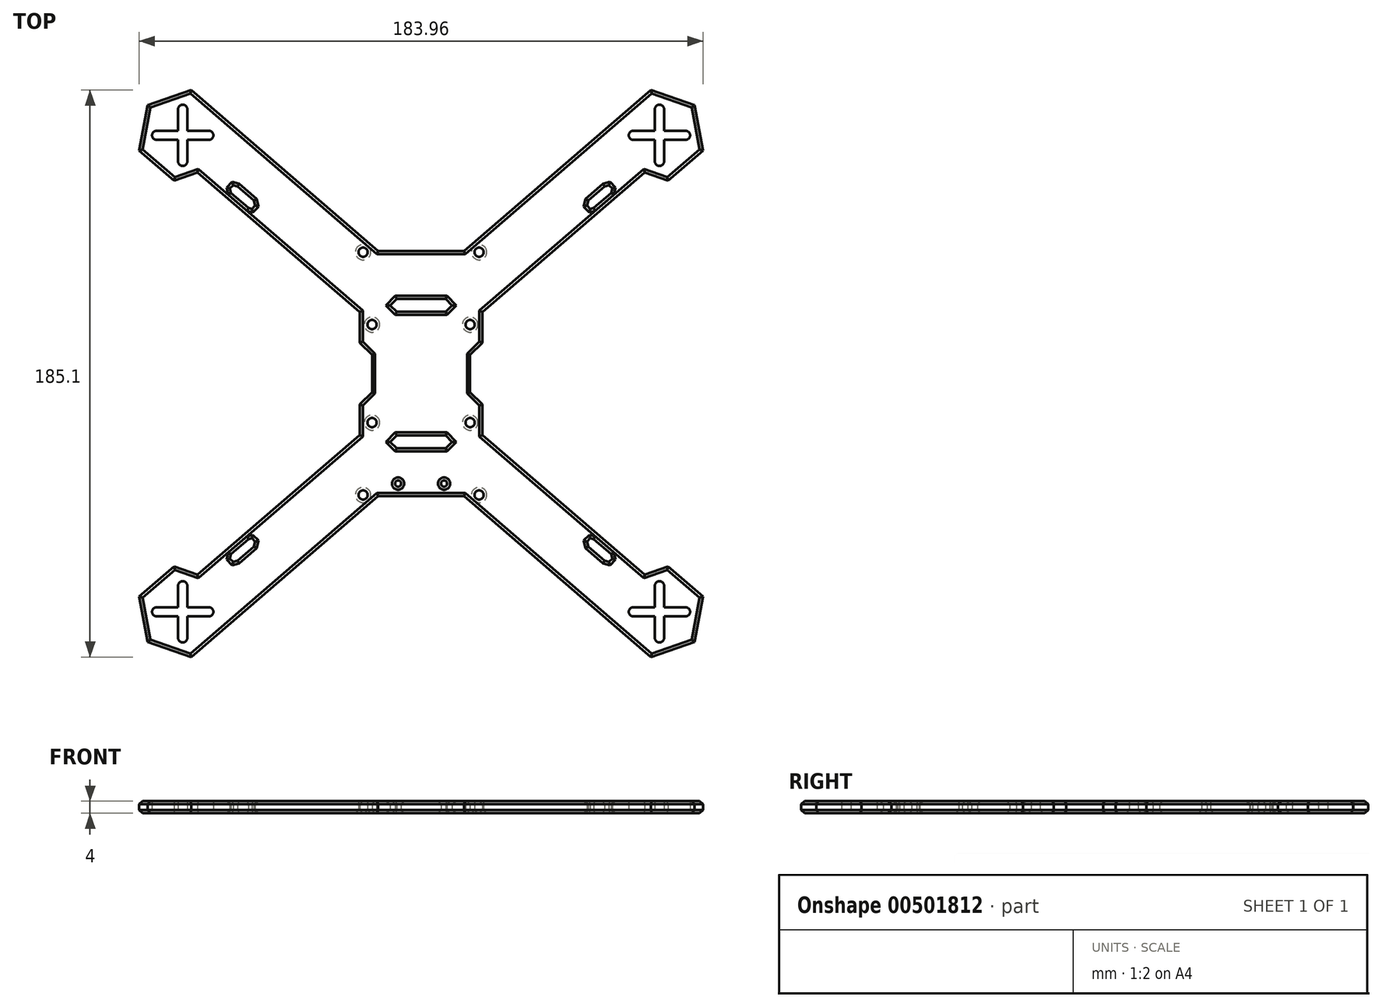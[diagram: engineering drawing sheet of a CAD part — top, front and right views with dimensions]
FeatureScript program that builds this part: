
annotation { "Feature Type Name" : "Feature", "Feature Type Description" : "" }
export const myFeature = defineFeature(function(context is Context, id is Id, definition is map)
    precondition{}
    {
        {
            var Q0;
            Q0=qCreatedBy(makeId("Top.planeOp"),FACE);
            var sketch = newSketch(context, id + "F0", { "sketchPlane" : qUnion([Q0])});
            skCircle(sketch, "E0", {"center": v(16, 16) * mm, "radius": 1.5 * mm});
            skPoint(sketch, "E1.middle", {"position": v(77.78, 77.78) * mm});
            skLineSegment(sketch, "E2.bottom", {"start": v(77.78, 67.78) * mm, "end": v(77.78, 67.78) * mm});
            skLineSegment(sketch, "E2.top", {"start": v(77.78, 87.78) * mm, "end": v(77.78, 87.78) * mm});
            skLineSegment(sketch, "E2.left", {"start": v(76.28, 69.28) * mm, "end": v(76.28, 76.29) * mm});
            skLineSegment(sketch, "E2.right", {"start": v(79.28, 69.28) * mm, "end": v(79.28, 76.28) * mm});
            skLineSegment(sketch, "E3.bottom", {"start": v(86.28, 79.28) * mm, "end": v(79.28, 79.28) * mm});
            skLineSegment(sketch, "E3.top", {"start": v(86.28, 76.28) * mm, "end": v(79.28, 76.28) * mm});
            skLineSegment(sketch, "E3.left", {"start": v(87.78, 77.78) * mm, "end": v(87.78, 77.78) * mm});
            skLineSegment(sketch, "E3.right", {"start": v(67.78, 77.78) * mm, "end": v(67.78, 77.78) * mm});
            skPoint(sketch, "E4.visualSharp", {"position": v(79.28, 87.78) * mm});
            skArc(sketch, "E4.filletArc", {"start": v(79.28, 86.28) * mm, "mid": v(78.84, 87.34) * mm, "end": v(77.78, 87.78) * mm});
            skPoint(sketch, "E5.visualSharp", {"position": v(76.28, 87.78) * mm});
            skArc(sketch, "E5.filletArc", {"start": v(77.78, 87.78) * mm, "mid": v(76.72, 87.34) * mm, "end": v(76.28, 86.28) * mm});
            skPoint(sketch, "E6.visualSharp", {"position": v(79.28, 67.78) * mm});
            skArc(sketch, "E6.filletArc", {"start": v(77.78, 67.78) * mm, "mid": v(78.84, 68.22) * mm, "end": v(79.28, 69.28) * mm});
            skPoint(sketch, "E7.visualSharp", {"position": v(76.28, 67.78) * mm});
            skArc(sketch, "E7.filletArc", {"start": v(76.28, 69.28) * mm, "mid": v(76.72, 68.22) * mm, "end": v(77.78, 67.78) * mm});
            skPoint(sketch, "E8.visualSharp", {"position": v(87.78, 79.28) * mm});
            skArc(sketch, "E8.filletArc", {"start": v(87.78, 77.78) * mm, "mid": v(87.34, 78.84) * mm, "end": v(86.28, 79.28) * mm});
            skPoint(sketch, "E9.visualSharp", {"position": v(87.78, 76.28) * mm});
            skArc(sketch, "E9.filletArc", {"start": v(86.28, 76.28) * mm, "mid": v(87.34, 76.72) * mm, "end": v(87.78, 77.78) * mm});
            skPoint(sketch, "E10.visualSharp", {"position": v(67.78, 79.28) * mm});
            skArc(sketch, "E10.filletArc", {"start": v(69.28, 79.28) * mm, "mid": v(68.22, 78.84) * mm, "end": v(67.78, 77.78) * mm});
            skPoint(sketch, "E11.visualSharp", {"position": v(67.78, 76.28) * mm});
            skArc(sketch, "E11.filletArc", {"start": v(67.78, 77.78) * mm, "mid": v(68.22, 76.72) * mm, "end": v(69.28, 76.28) * mm});
            skLineSegment(sketch, "E12.trimOffspring", {"start": v(76.28, 79.28) * mm, "end": v(76.28, 86.28) * mm});
            skLineSegment(sketch, "E13.trimOffspring", {"start": v(76.28, 76.28) * mm, "end": v(69.28, 76.28) * mm});
            skLineSegment(sketch, "E14.trimOffspring", {"start": v(76.28, 79.28) * mm, "end": v(69.28, 79.28) * mm});
            skLineSegment(sketch, "E15.trimOffspring", {"start": v(79.28, 79.28) * mm, "end": v(79.28, 86.28) * mm});
            skLineSegment(sketch, "E16.cCircle", {"start": v(49.17, 49.17) * mm, "end": v(49.17, 49.17) * mm});
            skLineSegment(sketch, "E17", {"start": v(77.78, 77.78) * mm, "end": v(0, 0) * mm, "construction": true});
            skLineSegment(sketch, "E18", {"start": v(69.28, 87.64) * mm, "end": v(14, 40) * mm});
            skLineSegment(sketch, "E19", {"start": v(20, 20.09) * mm, "end": v(72.91, 65.7) * mm});
            skLineSegment(sketch, "E20", {"start": v(20, 20.09) * mm, "end": v(20, 10.04) * mm});
            skLineSegment(sketch, "E21", {"start": v(14, 40) * mm, "end": v(0, 40) * mm});
            skLineSegment(sketch, "E22", {"start": v(61.99, 58.96) * mm, "end": v(56.29, 54.05) * mm});
            skCircle(sketch, "E23", {"center": v(77.78, 77.78) * mm, "radius": 63.5 * mm, "construction": true});
            skLineSegment(sketch, "E24", {"start": v(8, 20.17) * mm, "end": v(0, 20.17) * mm});
            skLineSegment(sketch, "E25", {"start": v(8, 20.17) * mm, "end": v(10.12, 22.3) * mm});
            skLineSegment(sketch, "E26", {"start": v(10.12, 22.3) * mm, "end": v(8, 24.41) * mm});
            skLineSegment(sketch, "E27", {"start": v(8, 24.41) * mm, "end": v(0, 24.41) * mm});
            skLineSegment(sketch, "E28", {"start": v(14, 40) * mm, "end": v(14, 0) * mm, "construction": true});
            skCircle(sketch, "E29", {"center": v(18.94, 39.63) * mm, "radius": 1.5 * mm});
            skLineSegment(sketch, "E30.3", {"start": v(59.86, 61.08) * mm, "end": v(61.31, 61.47) * mm});
            skLineSegment(sketch, "E30.4", {"start": v(61.31, 61.47) * mm, "end": v(62.37, 60.41) * mm});
            skLineSegment(sketch, "E30.5", {"start": v(62.37, 60.41) * mm, "end": v(61.99, 58.96) * mm});
            skLineSegment(sketch, "E31.0", {"start": v(56.29, 54.05) * mm, "end": v(55.18, 53.75) * mm});
            skLineSegment(sketch, "E31.1", {"start": v(55.18, 53.75) * mm, "end": v(54.12, 54.81) * mm});
            skLineSegment(sketch, "E31.2", {"start": v(54.12, 54.81) * mm, "end": v(54.56, 56.5) * mm});
            skLineSegment(sketch, "E32", {"start": v(14, 40) * mm, "end": v(21.57, 46.53) * mm, "construction": true});
            skLineSegment(sketch, "E33", {"start": v(21.57, 46.53) * mm, "end": v(26.14, 41.23) * mm, "construction": true});
            skLineSegment(sketch, "E34", {"start": v(26.14, 41.23) * mm, "end": v(18.57, 34.7) * mm, "construction": true});
            skLineSegment(sketch, "E35", {"start": v(18.57, 34.7) * mm, "end": v(14, 40) * mm, "construction": true});
            skLineSegment(sketch, "E36", {"start": v(59.86, 61.08) * mm, "end": v(54.56, 56.5) * mm});
            skPoint(sketch, "E37.0.midPoint", {"position": v(69.28, 87.64) * mm});
            skCircle(sketch, "E38.cCircle", {"center": v(77.78, 77.78) * mm, "radius": 13.02 * mm, "construction": true});
            skLineSegment(sketch, "E38.0", {"start": v(63.59, 82.74) * mm, "end": v(74.98, 92.55) * mm});
            skLineSegment(sketch, "E38.1", {"start": v(74.98, 92.55) * mm, "end": v(89.17, 87.6) * mm});
            skLineSegment(sketch, "E38.2", {"start": v(89.17, 87.6) * mm, "end": v(91.98, 72.83) * mm});
            skLineSegment(sketch, "E38.3", {"start": v(91.98, 72.83) * mm, "end": v(80.59, 63.01) * mm});
            skLineSegment(sketch, "E38.4", {"start": v(80.59, 63.01) * mm, "end": v(72.91, 65.7) * mm});
            skArc(sketch, "E39.MirrorCS", {"start": v(-79.28, 86.28) * mm, "mid": v(-78.84, 87.34) * mm, "end": v(-77.78, 87.78) * mm});
            skArc(sketch, "E40.MirrorCS", {"start": v(-77.78, 87.78) * mm, "mid": v(-76.72, 87.34) * mm, "end": v(-76.28, 86.28) * mm});
            skLineSegment(sketch, "E41.MirrorCS", {"start": v(-76.28, 79.28) * mm, "end": v(-76.28, 86.28) * mm});
            skLineSegment(sketch, "E42.MirrorCS", {"start": v(-76.28, 69.28) * mm, "end": v(-76.28, 76.29) * mm});
            skLineSegment(sketch, "E43.MirrorCS", {"start": v(-79.28, 69.28) * mm, "end": v(-79.28, 76.28) * mm});
            skLineSegment(sketch, "E44.MirrorCS", {"start": v(-86.28, 79.28) * mm, "end": v(-79.28, 79.28) * mm});
            skLineSegment(sketch, "E45.MirrorCS", {"start": v(-86.28, 76.28) * mm, "end": v(-79.28, 76.28) * mm});
            skArc(sketch, "E46.MirrorCS", {"start": v(-77.78, 67.78) * mm, "mid": v(-78.84, 68.22) * mm, "end": v(-79.28, 69.28) * mm});
            skArc(sketch, "E47.MirrorCS", {"start": v(-76.28, 69.28) * mm, "mid": v(-76.72, 68.22) * mm, "end": v(-77.78, 67.78) * mm});
            skArc(sketch, "E48.MirrorCS", {"start": v(-87.78, 77.78) * mm, "mid": v(-87.34, 78.84) * mm, "end": v(-86.28, 79.28) * mm});
            skArc(sketch, "E49.MirrorCS", {"start": v(-86.28, 76.28) * mm, "mid": v(-87.34, 76.72) * mm, "end": v(-87.78, 77.78) * mm});
            skArc(sketch, "E50.MirrorCS", {"start": v(-69.28, 79.28) * mm, "mid": v(-68.22, 78.84) * mm, "end": v(-67.78, 77.78) * mm});
            skArc(sketch, "E51.MirrorCS", {"start": v(-67.78, 77.78) * mm, "mid": v(-68.22, 76.72) * mm, "end": v(-69.28, 76.28) * mm});
            skLineSegment(sketch, "E52.MirrorCS", {"start": v(-79.28, 79.28) * mm, "end": v(-79.28, 86.28) * mm});
            skLineSegment(sketch, "E53.MirrorCS", {"start": v(-10.12, 22.3) * mm, "end": v(-8, 24.41) * mm});
            skPoint(sketch, "E54.MirrorP", {"position": v(-77.78, 77.78) * mm});
            skLineSegment(sketch, "E55.MirrorCS", {"start": v(-8, 20.17) * mm, "end": v(-10.12, 22.3) * mm});
            skLineSegment(sketch, "E56.MirrorCS", {"start": v(-55.18, 53.75) * mm, "end": v(-54.12, 54.81) * mm});
            skLineSegment(sketch, "E57.MirrorCS", {"start": v(-54.12, 54.81) * mm, "end": v(-54.56, 56.5) * mm});
            skLineSegment(sketch, "E58.MirrorCS", {"start": v(-76.28, 76.28) * mm, "end": v(-69.28, 76.28) * mm});
            skLineSegment(sketch, "E59.MirrorCS", {"start": v(-76.28, 79.28) * mm, "end": v(-69.28, 79.28) * mm});
            skCircle(sketch, "E60.MirrorC", {"center": v(-16, 16) * mm, "radius": 1.5 * mm});
            skLineSegment(sketch, "E61.MirrorCS", {"start": v(-18.57, 34.7) * mm, "end": v(-14, 40) * mm, "construction": true});
            skCircle(sketch, "E62.MirrorC", {"center": v(-18.94, 39.63) * mm, "radius": 1.5 * mm});
            skLineSegment(sketch, "E63.MirrorCS", {"start": v(-62.37, 60.41) * mm, "end": v(-61.99, 58.96) * mm});
            skLineSegment(sketch, "E64.MirrorCS", {"start": v(-59.86, 61.08) * mm, "end": v(-54.56, 56.5) * mm});
            skLineSegment(sketch, "E65.MirrorCS", {"start": v(-80.59, 63.01) * mm, "end": v(-72.91, 65.7) * mm});
            skLineSegment(sketch, "E66.MirrorCS", {"start": v(-59.86, 61.08) * mm, "end": v(-61.31, 61.47) * mm});
            skLineSegment(sketch, "E67.MirrorCS", {"start": v(-21.57, 46.53) * mm, "end": v(-26.14, 41.23) * mm, "construction": true});
            skLineSegment(sketch, "E68.MirrorCS", {"start": v(-56.29, 54.05) * mm, "end": v(-55.18, 53.75) * mm});
            skLineSegment(sketch, "E69.MirrorCS", {"start": v(-61.99, 58.96) * mm, "end": v(-56.29, 54.05) * mm});
            skLineSegment(sketch, "E70.MirrorCS", {"start": v(-61.31, 61.47) * mm, "end": v(-62.37, 60.41) * mm});
            skLineSegment(sketch, "E71.MirrorCS", {"start": v(-63.59, 82.74) * mm, "end": v(-74.98, 92.55) * mm});
            skPoint(sketch, "E72.MirrorP", {"position": v(-69.28, 87.64) * mm});
            skLineSegment(sketch, "E73.MirrorCS", {"start": v(-8, 24.41) * mm, "end": v(0, 24.41) * mm});
            skLineSegment(sketch, "E74.MirrorCS", {"start": v(-14, 40) * mm, "end": v(-21.57, 46.53) * mm, "construction": true});
            skLineSegment(sketch, "E75.MirrorCS", {"start": v(-89.17, 87.6) * mm, "end": v(-91.98, 72.83) * mm});
            skLineSegment(sketch, "E76.MirrorCS", {"start": v(-20, 20.09) * mm, "end": v(-72.91, 65.7) * mm});
            skPoint(sketch, "E77.MirrorP", {"position": v(-79.28, 87.78) * mm});
            skPoint(sketch, "E78.MirrorP", {"position": v(-87.78, 76.28) * mm});
            skLineSegment(sketch, "E79.MirrorCS", {"start": v(-74.98, 92.55) * mm, "end": v(-89.17, 87.6) * mm});
            skCircle(sketch, "E80.MirrorC", {"center": v(-77.78, 77.78) * mm, "radius": 63.5 * mm, "construction": true});
            skPoint(sketch, "E81.MirrorP", {"position": v(-76.28, 67.78) * mm});
            skLineSegment(sketch, "E82.MirrorCS", {"start": v(-91.98, 72.83) * mm, "end": v(-80.59, 63.01) * mm});
            skPoint(sketch, "E83.MirrorP", {"position": v(-79.28, 67.78) * mm});
            skLineSegment(sketch, "E84.MirrorCS", {"start": v(-14, 40) * mm, "end": v(-14, 0) * mm, "construction": true});
            skLineSegment(sketch, "E85.MirrorCS", {"start": v(-8, 20.17) * mm, "end": v(0, 20.17) * mm});
            skLineSegment(sketch, "E86.MirrorCS", {"start": v(-14, 40) * mm, "end": v(0, 40) * mm});
            skPoint(sketch, "E87.MirrorP", {"position": v(-76.28, 87.78) * mm});
            skLineSegment(sketch, "E88.MirrorCS", {"start": v(-26.14, 41.23) * mm, "end": v(-18.57, 34.7) * mm, "construction": true});
            skLineSegment(sketch, "E89.MirrorCS", {"start": v(-77.78, 77.78) * mm, "end": v(0, 0) * mm, "construction": true});
            skPoint(sketch, "E90.MirrorP", {"position": v(-67.78, 76.28) * mm});
            skPoint(sketch, "E91.MirrorP", {"position": v(-67.78, 79.28) * mm});
            skPoint(sketch, "E92.MirrorP", {"position": v(-87.78, 79.28) * mm});
            skCircle(sketch, "E93.MirrorC", {"center": v(-77.78, 77.78) * mm, "radius": 13.02 * mm, "construction": true});
            skLineSegment(sketch, "E94.MirrorCS", {"start": v(-69.28, 87.64) * mm, "end": v(-14, 40) * mm});
            skArc(sketch, "E95.MirrorCS", {"start": v(76.28, -69.28) * mm, "mid": v(76.72, -68.22) * mm, "end": v(77.78, -67.78) * mm});
            skArc(sketch, "E96.MirrorCS", {"start": v(77.78, -67.78) * mm, "mid": v(78.84, -68.22) * mm, "end": v(79.28, -69.28) * mm});
            skArc(sketch, "E97.MirrorCS", {"start": v(77.78, -87.78) * mm, "mid": v(76.72, -87.34) * mm, "end": v(76.28, -86.28) * mm});
            skArc(sketch, "E98.MirrorCS", {"start": v(79.28, -86.28) * mm, "mid": v(78.84, -87.34) * mm, "end": v(77.78, -87.78) * mm});
            skLineSegment(sketch, "E99.MirrorCS", {"start": v(76.28, -79.28) * mm, "end": v(76.28, -86.28) * mm});
            skLineSegment(sketch, "E100.MirrorCS", {"start": v(-76.28, -79.28) * mm, "end": v(-76.28, -86.28) * mm});
            skArc(sketch, "E101.MirrorCS", {"start": v(-77.78, -87.78) * mm, "mid": v(-76.72, -87.34) * mm, "end": v(-76.28, -86.28) * mm});
            skLineSegment(sketch, "E102.MirrorCS", {"start": v(79.28, -79.28) * mm, "end": v(79.28, -86.28) * mm});
            skArc(sketch, "E103.MirrorCS", {"start": v(67.78, -77.78) * mm, "mid": v(68.22, -76.72) * mm, "end": v(69.28, -76.28) * mm});
            skArc(sketch, "E104.MirrorCS", {"start": v(69.28, -79.28) * mm, "mid": v(68.22, -78.84) * mm, "end": v(67.78, -77.78) * mm});
            skArc(sketch, "E105.MirrorCS", {"start": v(86.28, -76.28) * mm, "mid": v(87.34, -76.72) * mm, "end": v(87.78, -77.78) * mm});
            skArc(sketch, "E106.MirrorCS", {"start": v(87.78, -77.78) * mm, "mid": v(87.34, -78.84) * mm, "end": v(86.28, -79.28) * mm});
            skLineSegment(sketch, "E107.MirrorCS", {"start": v(86.28, -76.28) * mm, "end": v(79.28, -76.28) * mm});
            skLineSegment(sketch, "E108.MirrorCS", {"start": v(79.28, -69.28) * mm, "end": v(79.28, -76.28) * mm});
            skLineSegment(sketch, "E109.MirrorCS", {"start": v(76.28, -69.28) * mm, "end": v(76.28, -76.29) * mm});
            skLineSegment(sketch, "E110.MirrorCS", {"start": v(76.28, -79.28) * mm, "end": v(69.28, -79.28) * mm});
            skLineSegment(sketch, "E111.MirrorCS", {"start": v(76.28, -76.28) * mm, "end": v(69.28, -76.28) * mm});
            skArc(sketch, "E112.MirrorCS", {"start": v(-79.28, -86.28) * mm, "mid": v(-78.84, -87.34) * mm, "end": v(-77.78, -87.78) * mm});
            skLineSegment(sketch, "E113.MirrorCS", {"start": v(-79.28, -79.28) * mm, "end": v(-79.28, -86.28) * mm});
            skArc(sketch, "E114.MirrorCS", {"start": v(-86.28, -76.28) * mm, "mid": v(-87.34, -76.72) * mm, "end": v(-87.78, -77.78) * mm});
            skArc(sketch, "E115.MirrorCS", {"start": v(-87.78, -77.78) * mm, "mid": v(-87.34, -78.84) * mm, "end": v(-86.28, -79.28) * mm});
            skArc(sketch, "E116.MirrorCS", {"start": v(-76.28, -69.28) * mm, "mid": v(-76.72, -68.22) * mm, "end": v(-77.78, -67.78) * mm});
            skLineSegment(sketch, "E117.MirrorCS", {"start": v(86.28, -79.28) * mm, "end": v(79.28, -79.28) * mm});
            skArc(sketch, "E118.MirrorCS", {"start": v(-77.78, -67.78) * mm, "mid": v(-78.84, -68.22) * mm, "end": v(-79.28, -69.28) * mm});
            skLineSegment(sketch, "E119.MirrorCS", {"start": v(-86.28, -79.28) * mm, "end": v(-79.28, -79.28) * mm});
            skArc(sketch, "E120.MirrorCS", {"start": v(-67.78, -77.78) * mm, "mid": v(-68.22, -76.72) * mm, "end": v(-69.28, -76.28) * mm});
            skPoint(sketch, "E121.MirrorP", {"position": v(77.78, -77.78) * mm});
            skLineSegment(sketch, "E122.MirrorCS", {"start": v(-86.28, -76.28) * mm, "end": v(-79.28, -76.28) * mm});
            skLineSegment(sketch, "E123.MirrorCS", {"start": v(54.12, -54.81) * mm, "end": v(54.56, -56.5) * mm});
            skArc(sketch, "E124.MirrorCS", {"start": v(-69.28, -79.28) * mm, "mid": v(-68.22, -78.84) * mm, "end": v(-67.78, -77.78) * mm});
            skLineSegment(sketch, "E125.MirrorCS", {"start": v(55.18, -53.75) * mm, "end": v(54.12, -54.81) * mm});
            skLineSegment(sketch, "E126.MirrorCS", {"start": v(-76.28, -69.28) * mm, "end": v(-76.28, -76.29) * mm});
            skLineSegment(sketch, "E127.MirrorCS", {"start": v(-59.86, -61.08) * mm, "end": v(-61.31, -61.47) * mm});
            skLineSegment(sketch, "E128.MirrorCS", {"start": v(8, -20.17) * mm, "end": v(10.12, -22.3) * mm});
            skLineSegment(sketch, "E129.MirrorCS", {"start": v(56.29, -54.05) * mm, "end": v(55.18, -53.75) * mm});
            skLineSegment(sketch, "E130.MirrorCS", {"start": v(-80.59, -63.01) * mm, "end": v(-72.91, -65.7) * mm});
            skLineSegment(sketch, "E131.MirrorCS", {"start": v(59.86, -61.08) * mm, "end": v(54.56, -56.5) * mm});
            skLineSegment(sketch, "E132.MirrorCS", {"start": v(62.37, -60.41) * mm, "end": v(61.99, -58.96) * mm});
            skLineSegment(sketch, "E133.MirrorCS", {"start": v(-54.12, -54.81) * mm, "end": v(-54.56, -56.5) * mm});
            skLineSegment(sketch, "E134.MirrorCS", {"start": v(-59.86, -61.08) * mm, "end": v(-54.56, -56.5) * mm});
            skLineSegment(sketch, "E135.MirrorCS", {"start": v(18.57, -34.7) * mm, "end": v(14, -40) * mm, "construction": true});
            skCircle(sketch, "E136.MirrorC", {"center": v(16, -16) * mm, "radius": 1.5 * mm});
            skLineSegment(sketch, "E137.MirrorCS", {"start": v(61.31, -61.47) * mm, "end": v(62.37, -60.41) * mm});
            skLineSegment(sketch, "E138.MirrorCS", {"start": v(-62.37, -60.41) * mm, "end": v(-61.99, -58.96) * mm});
            skLineSegment(sketch, "E139.MirrorCS", {"start": v(-55.18, -53.75) * mm, "end": v(-54.12, -54.81) * mm});
            skLineSegment(sketch, "E140.MirrorCS", {"start": v(61.99, -58.96) * mm, "end": v(56.29, -54.05) * mm});
            skLineSegment(sketch, "E141.MirrorCS", {"start": v(-10.12, -22.3) * mm, "end": v(-8, -24.41) * mm});
            skLineSegment(sketch, "E142.MirrorCS", {"start": v(-18.57, -34.7) * mm, "end": v(-14, -40) * mm, "construction": true});
            skLineSegment(sketch, "E143.MirrorCS", {"start": v(-61.31, -61.47) * mm, "end": v(-62.37, -60.41) * mm});
            skLineSegment(sketch, "E144.MirrorCS", {"start": v(-56.29, -54.05) * mm, "end": v(-55.18, -53.75) * mm});
            skLineSegment(sketch, "E145.MirrorCS", {"start": v(21.57, -46.53) * mm, "end": v(26.14, -41.23) * mm, "construction": true});
            skLineSegment(sketch, "E146.MirrorCS", {"start": v(59.86, -61.08) * mm, "end": v(61.31, -61.47) * mm});
            skLineSegment(sketch, "E147.MirrorCS", {"start": v(80.59, -63.01) * mm, "end": v(72.91, -65.7) * mm});
            skLineSegment(sketch, "E148.MirrorCS", {"start": v(-8, -20.17) * mm, "end": v(-10.12, -22.3) * mm});
            skLineSegment(sketch, "E149.MirrorCS", {"start": v(-61.99, -58.96) * mm, "end": v(-56.29, -54.05) * mm});
            skLineSegment(sketch, "E150.MirrorCS", {"start": v(-79.28, -69.28) * mm, "end": v(-79.28, -76.28) * mm});
            skLineSegment(sketch, "E151.MirrorCS", {"start": v(-21.57, -46.53) * mm, "end": v(-26.14, -41.23) * mm, "construction": true});
            skLineSegment(sketch, "E152.MirrorCS", {"start": v(10.12, -22.3) * mm, "end": v(8, -24.41) * mm});
            skPoint(sketch, "E153.MirrorP", {"position": v(-77.78, -77.78) * mm});
            skLineSegment(sketch, "E154.MirrorCS", {"start": v(-89.17, -87.6) * mm, "end": v(-91.98, -72.83) * mm});
            skLineSegment(sketch, "E155.MirrorCS", {"start": v(26.14, -41.23) * mm, "end": v(18.57, -34.7) * mm, "construction": true});
            skCircle(sketch, "E156.MirrorC", {"center": v(18.94, -39.63) * mm, "radius": 1.5 * mm});
            skLineSegment(sketch, "E157.MirrorCS", {"start": v(14, -40) * mm, "end": v(21.57, -46.53) * mm, "construction": true});
            skLineSegment(sketch, "E158.MirrorCS", {"start": v(8, -24.41) * mm, "end": v(0, -24.41) * mm});
            skCircle(sketch, "E159.MirrorC", {"center": v(-18.94, -39.63) * mm, "radius": 1.5 * mm});
            skLineSegment(sketch, "E160.MirrorCS", {"start": v(-63.59, -82.74) * mm, "end": v(-74.98, -92.55) * mm});
            skLineSegment(sketch, "E161.MirrorCS", {"start": v(14, -40) * mm, "end": v(0, -40) * mm});
            skLineSegment(sketch, "E162.MirrorCS", {"start": v(89.17, -87.6) * mm, "end": v(91.98, -72.83) * mm});
            skCircle(sketch, "E163.MirrorC", {"center": v(-16, -16) * mm, "radius": 1.5 * mm});
            skLineSegment(sketch, "E164.MirrorCS", {"start": v(-26.14, -41.23) * mm, "end": v(-18.57, -34.7) * mm, "construction": true});
            skLineSegment(sketch, "E165.MirrorCS", {"start": v(63.59, -82.74) * mm, "end": v(74.98, -92.55) * mm});
            skPoint(sketch, "E166.MirrorP", {"position": v(69.28, -87.64) * mm});
            skPoint(sketch, "E167.MirrorP", {"position": v(-69.28, -87.64) * mm});
            skPoint(sketch, "E168.MirrorP", {"position": v(-76.28, -87.78) * mm});
            skLineSegment(sketch, "E169.MirrorCS", {"start": v(-76.28, -79.28) * mm, "end": v(-69.28, -79.28) * mm});
            skLineSegment(sketch, "E170.MirrorCS", {"start": v(-20, -20.09) * mm, "end": v(-72.91, -65.7) * mm});
            skLineSegment(sketch, "E171.MirrorCS", {"start": v(69.28, -87.64) * mm, "end": v(14, -40) * mm});
            skLineSegment(sketch, "E172.MirrorCS", {"start": v(-14, -40) * mm, "end": v(0, -40) * mm});
            skCircle(sketch, "E173.MirrorC", {"center": v(77.78, -77.78) * mm, "radius": 13.02 * mm, "construction": true});
            skPoint(sketch, "E174.MirrorP", {"position": v(76.28, -87.78) * mm});
            skLineSegment(sketch, "E175.MirrorCS", {"start": v(-76.28, -76.28) * mm, "end": v(-69.28, -76.28) * mm});
            skLineSegment(sketch, "E176.MirrorCS", {"start": v(77.78, -77.78) * mm, "end": v(0, 0) * mm, "construction": true});
            skLineSegment(sketch, "E177.MirrorCS", {"start": v(-8, -20.17) * mm, "end": v(0, -20.17) * mm});
            skLineSegment(sketch, "E178.MirrorCS", {"start": v(8, -20.17) * mm, "end": v(0, -20.17) * mm});
            skPoint(sketch, "E179.MirrorP", {"position": v(87.78, -79.28) * mm});
            skPoint(sketch, "E180.MirrorP", {"position": v(-79.28, -67.78) * mm});
            skLineSegment(sketch, "E181.MirrorCS", {"start": v(-14, -40) * mm, "end": v(-21.57, -46.53) * mm, "construction": true});
            skPoint(sketch, "E182.MirrorP", {"position": v(79.28, -87.78) * mm});
            skLineSegment(sketch, "E183.MirrorCS", {"start": v(-14, -40) * mm, "end": v(-14, 0) * mm, "construction": true});
            skCircle(sketch, "E184.MirrorC", {"center": v(77.78, -77.78) * mm, "radius": 63.5 * mm, "construction": true});
            skPoint(sketch, "E185.MirrorP", {"position": v(-76.28, -67.78) * mm});
            skLineSegment(sketch, "E186.MirrorCS", {"start": v(-91.98, -72.83) * mm, "end": v(-80.59, -63.01) * mm});
            skLineSegment(sketch, "E187.MirrorCS", {"start": v(-8, -24.41) * mm, "end": v(0, -24.41) * mm});
            skPoint(sketch, "E188.MirrorP", {"position": v(76.28, -67.78) * mm});
            skLineSegment(sketch, "E189.MirrorCS", {"start": v(91.98, -72.83) * mm, "end": v(80.59, -63.01) * mm});
            skPoint(sketch, "E190.MirrorP", {"position": v(67.78, -79.28) * mm});
            skPoint(sketch, "E191.MirrorP", {"position": v(-67.78, -79.28) * mm});
            skCircle(sketch, "E192.MirrorC", {"center": v(-77.78, -77.78) * mm, "radius": 63.5 * mm, "construction": true});
            skLineSegment(sketch, "E193.MirrorCS", {"start": v(20, -20.09) * mm, "end": v(20, -10.04) * mm});
            skLineSegment(sketch, "E194.MirrorCS", {"start": v(14, -40) * mm, "end": v(14, 0) * mm, "construction": true});
            skLineSegment(sketch, "E195.MirrorCS", {"start": v(-77.78, -77.78) * mm, "end": v(0, 0) * mm, "construction": true});
            skLineSegment(sketch, "E196.MirrorCS", {"start": v(74.98, -92.55) * mm, "end": v(89.17, -87.6) * mm});
            skPoint(sketch, "E197.MirrorP", {"position": v(-79.28, -87.78) * mm});
            skPoint(sketch, "E198.MirrorP", {"position": v(-87.78, -79.28) * mm});
            skPoint(sketch, "E199.MirrorP", {"position": v(79.28, -67.78) * mm});
            skPoint(sketch, "E200.MirrorP", {"position": v(87.78, -76.28) * mm});
            skPoint(sketch, "E201.MirrorP", {"position": v(-67.78, -76.28) * mm});
            skCircle(sketch, "E202.MirrorC", {"center": v(-77.78, -77.78) * mm, "radius": 13.02 * mm, "construction": true});
            skPoint(sketch, "E203.MirrorP", {"position": v(-87.78, -76.28) * mm});
            skPoint(sketch, "E204.MirrorP", {"position": v(67.78, -76.28) * mm});
            skLineSegment(sketch, "E205.MirrorCS", {"start": v(-74.98, -92.55) * mm, "end": v(-89.17, -87.6) * mm});
            skLineSegment(sketch, "E206.MirrorCS", {"start": v(20, -20.09) * mm, "end": v(72.91, -65.7) * mm});
            skLineSegment(sketch, "E207.MirrorCS", {"start": v(-69.28, -87.64) * mm, "end": v(-14, -40) * mm});
            skCircle(sketch, "E208", {"center": v(7.5, -35.92) * mm, "radius": 1 * mm});
            skCircle(sketch, "E209.MirrorC", {"center": v(-7.5, -35.92) * mm, "radius": 1 * mm});
            skLineSegment(sketch, "E210", {"start": v(20, -10.04) * mm, "end": v(16, -6.04) * mm});
            skLineSegment(sketch, "E211", {"start": v(16, -6.04) * mm, "end": v(16, 0) * mm});
            skLineSegment(sketch, "E212.MirrorCS", {"start": v(20, 10.04) * mm, "end": v(16, 6.04) * mm});
            skLineSegment(sketch, "E213.MirrorCS", {"start": v(16, 6.04) * mm, "end": v(16, 0) * mm});
            skLineSegment(sketch, "E214.MirrorCS", {"start": v(-20, 20.09) * mm, "end": v(-20, 10.04) * mm});
            skLineSegment(sketch, "E215.MirrorCS", {"start": v(-16, 6.04) * mm, "end": v(-16, 0) * mm});
            skLineSegment(sketch, "E216.MirrorCS", {"start": v(-20, -20.09) * mm, "end": v(-20, -10.04) * mm});
            skLineSegment(sketch, "E217.MirrorCS", {"start": v(-20, -10.04) * mm, "end": v(-16, -6.04) * mm});
            skLineSegment(sketch, "E218.MirrorCS", {"start": v(-16, -6.04) * mm, "end": v(-16, 0) * mm});
            skLineSegment(sketch, "E219.MirrorCS", {"start": v(-20, 10.04) * mm, "end": v(-16, 6.04) * mm});
            skLineSegment(sketch, "E220", {"start": v(-89.17, 92.55) * mm, "end": v(91.98, 92.55) * mm, "construction": true});
            skLineSegment(sketch, "E221", {"start": v(91.98, 92.55) * mm, "end": v(91.98, -92.55) * mm, "construction": true});
            skLineSegment(sketch, "E222", {"start": v(91.75, -93.86) * mm, "end": v(-89.17, -93.86) * mm, "construction": true});
            skLineSegment(sketch, "E223", {"start": v(-90, -95.26) * mm, "end": v(-89.17, 92.55) * mm, "construction": true});
            skSolve(sketch);
        }
        {
            var Q0;
            Q0=makeQuery(id+"F0.imprint","IMPRINT",FACE,{"disambiguationData":[TD([[makeQuery(id+"F0.imprint","IMPRINT",EDGE,{"derivedFrom":sQuery(id+"F0.wireOp",EDGE,"E0")}),-1.0]])]});
            extrude(context, id + "F1", {"entities" : qUnion([Q0]), "depth" : 4 * mm});
        }
        {
            var Q0;
            Q0=makeQuery(id+"F1.opExtrude","CAP_EDGE",EDGE,{"disambiguationData":[OSD([sQuery(id+"F0.wireOp",EDGE,"E60.MirrorC")])],"isStart":true});
            var Q1;
            Q1=makeQuery(id+"F1.opExtrude","CAP_EDGE",EDGE,{"disambiguationData":[OSD([sQuery(id+"F0.wireOp",EDGE,"E136.MirrorC")])],"isStart":true});
            var Q2;
            Q2=makeQuery(id+"F1.opExtrude","CAP_EDGE",EDGE,{"disambiguationData":[OSD([sQuery(id+"F0.wireOp",EDGE,"E163.MirrorC")])],"isStart":true});
            var Q3;
            Q3=makeQuery(id+"F1.opExtrude","CAP_EDGE",EDGE,{"disambiguationData":[OSD([sQuery(id+"F0.wireOp",EDGE,"E0")])],"isStart":true});
            var Q4;
            Q4=makeQuery(id+"F1.opExtrude","CAP_EDGE",EDGE,{"disambiguationData":[OSD([sQuery(id+"F0.wireOp",EDGE,"E62.MirrorC")])],"isStart":true});
            var Q5;
            Q5=makeQuery(id+"F1.opExtrude","CAP_EDGE",EDGE,{"disambiguationData":[OSD([sQuery(id+"F0.wireOp",EDGE,"E29")])],"isStart":true});
            var Q6;
            Q6=makeQuery(id+"F1.opExtrude","CAP_EDGE",EDGE,{"disambiguationData":[OSD([sQuery(id+"F0.wireOp",EDGE,"E156.MirrorC")])],"isStart":true});
            var Q7;
            Q7=makeQuery(id+"F1.opExtrude","CAP_EDGE",EDGE,{"disambiguationData":[OSD([sQuery(id+"F0.wireOp",EDGE,"E159.MirrorC")])],"isStart":true});
            chamfer(context, id + "F2", {"entities" : qUnion([Q0, Q1, Q2, Q3, Q4, Q5, Q6, Q7]), "width" : 1 * mm, "tangentPropagation" : true});
        }
        {
            var Q0;
            Q0=makeQuery(id+"F1.opExtrude","CAP_EDGE",EDGE,{"disambiguationData":[OSD([sQuery(id+"F0.wireOp",EDGE,"E128.MirrorCS")])],"isStart":true});
            var Q1;
            Q1=makeQuery(id+"F1.opExtrude","CAP_EDGE",EDGE,{"disambiguationData":[OSD([sQuery(id+"F0.wireOp",EDGE,"E152.MirrorCS")])],"isStart":true});
            var Q2;
            Q2=makeQuery(id+"F1.opExtrude","CAP_EDGE",EDGE,{"disambiguationData":[OSD([sQuery(id+"F0.wireOp",EDGE,"E177.MirrorCS"),sQuery(id+"F0.wireOp",EDGE,"E178.MirrorCS")])],"isStart":true});
            var Q3;
            Q3=makeQuery(id+"F1.opExtrude","CAP_EDGE",EDGE,{"disambiguationData":[OSD([sQuery(id+"F0.wireOp",EDGE,"E148.MirrorCS")])],"isStart":true});
            var Q4;
            Q4=makeQuery(id+"F1.opExtrude","CAP_EDGE",EDGE,{"disambiguationData":[OSD([sQuery(id+"F0.wireOp",EDGE,"E141.MirrorCS")])],"isStart":true});
            var Q5;
            Q5=makeQuery(id+"F1.opExtrude","CAP_EDGE",EDGE,{"disambiguationData":[OSD([sQuery(id+"F0.wireOp",EDGE,"E158.MirrorCS"),sQuery(id+"F0.wireOp",EDGE,"E187.MirrorCS")])],"isStart":true});
            var Q6;
            Q6=makeQuery(id+"F1.opExtrude","CAP_EDGE",EDGE,{"disambiguationData":[OSD([sQuery(id+"F0.wireOp",EDGE,"E27"),sQuery(id+"F0.wireOp",EDGE,"E73.MirrorCS")])],"isStart":true});
            var Q7;
            Q7=makeQuery(id+"F1.opExtrude","CAP_EDGE",EDGE,{"disambiguationData":[OSD([sQuery(id+"F0.wireOp",EDGE,"E26")])],"isStart":true});
            var Q8;
            Q8=makeQuery(id+"F1.opExtrude","CAP_EDGE",EDGE,{"disambiguationData":[OSD([sQuery(id+"F0.wireOp",EDGE,"E25")])],"isStart":true});
            var Q9;
            Q9=makeQuery(id+"F1.opExtrude","CAP_EDGE",EDGE,{"disambiguationData":[OSD([sQuery(id+"F0.wireOp",EDGE,"E24"),sQuery(id+"F0.wireOp",EDGE,"E85.MirrorCS")])],"isStart":true});
            var Q10;
            Q10=makeQuery(id+"F1.opExtrude","CAP_EDGE",EDGE,{"disambiguationData":[OSD([sQuery(id+"F0.wireOp",EDGE,"E55.MirrorCS")])],"isStart":true});
            var Q11;
            Q11=makeQuery(id+"F1.opExtrude","CAP_EDGE",EDGE,{"disambiguationData":[OSD([sQuery(id+"F0.wireOp",EDGE,"E53.MirrorCS")])],"isStart":true});
            chamfer(context, id + "F3", {"entities" : qUnion([Q0, Q1, Q2, Q3, Q4, Q5, Q6, Q7, Q8, Q9, Q10, Q11]), "width" : 1 * mm, "tangentPropagation" : true});
        }
        {
            var Q0;
            Q0=makeQuery(id+"F1.opExtrude","CAP_EDGE",EDGE,{"disambiguationData":[OSD([sQuery(id+"F0.wireOp",EDGE,"E53.MirrorCS")])],"isStart":false});
            var Q1;
            Q1=makeQuery(id+"F1.opExtrude","CAP_EDGE",EDGE,{"disambiguationData":[OSD([sQuery(id+"F0.wireOp",EDGE,"E55.MirrorCS")])],"isStart":false});
            var Q2;
            Q2=makeQuery(id+"F1.opExtrude","CAP_EDGE",EDGE,{"disambiguationData":[OSD([sQuery(id+"F0.wireOp",EDGE,"E24"),sQuery(id+"F0.wireOp",EDGE,"E85.MirrorCS")])],"isStart":false});
            var Q3;
            Q3=makeQuery(id+"F1.opExtrude","CAP_EDGE",EDGE,{"disambiguationData":[OSD([sQuery(id+"F0.wireOp",EDGE,"E27"),sQuery(id+"F0.wireOp",EDGE,"E73.MirrorCS")])],"isStart":false});
            var Q4;
            Q4=makeQuery(id+"F1.opExtrude","CAP_EDGE",EDGE,{"disambiguationData":[OSD([sQuery(id+"F0.wireOp",EDGE,"E26")])],"isStart":false});
            var Q5;
            Q5=makeQuery(id+"F1.opExtrude","CAP_EDGE",EDGE,{"disambiguationData":[OSD([sQuery(id+"F0.wireOp",EDGE,"E25")])],"isStart":false});
            var Q6;
            Q6=makeQuery(id+"F1.opExtrude","CAP_EDGE",EDGE,{"disambiguationData":[OSD([sQuery(id+"F0.wireOp",EDGE,"E148.MirrorCS")])],"isStart":false});
            var Q7;
            Q7=makeQuery(id+"F1.opExtrude","CAP_EDGE",EDGE,{"disambiguationData":[OSD([sQuery(id+"F0.wireOp",EDGE,"E141.MirrorCS")])],"isStart":false});
            var Q8;
            Q8=makeQuery(id+"F1.opExtrude","CAP_EDGE",EDGE,{"disambiguationData":[OSD([sQuery(id+"F0.wireOp",EDGE,"E177.MirrorCS"),sQuery(id+"F0.wireOp",EDGE,"E178.MirrorCS")])],"isStart":false});
            var Q9;
            Q9=makeQuery(id+"F1.opExtrude","CAP_EDGE",EDGE,{"disambiguationData":[OSD([sQuery(id+"F0.wireOp",EDGE,"E158.MirrorCS"),sQuery(id+"F0.wireOp",EDGE,"E187.MirrorCS")])],"isStart":false});
            var Q10;
            Q10=makeQuery(id+"F1.opExtrude","CAP_EDGE",EDGE,{"disambiguationData":[OSD([sQuery(id+"F0.wireOp",EDGE,"E152.MirrorCS")])],"isStart":false});
            var Q11;
            Q11=makeQuery(id+"F1.opExtrude","CAP_EDGE",EDGE,{"disambiguationData":[OSD([sQuery(id+"F0.wireOp",EDGE,"E128.MirrorCS")])],"isStart":false});
            chamfer(context, id + "F4", {"entities" : qUnion([Q0, Q1, Q2, Q3, Q4, Q5, Q6, Q7, Q8, Q9, Q10, Q11]), "width" : 1 * mm, "tangentPropagation" : true});
        }
        {
            var Q0;
            Q0=makeQuery(id+"F1.opExtrude","CAP_EDGE",EDGE,{"disambiguationData":[OSD([sQuery(id+"F0.wireOp",EDGE,"E36")])],"isStart":false});
            var Q1;
            Q1=makeQuery(id+"F1.opExtrude","CAP_EDGE",EDGE,{"disambiguationData":[OSD([sQuery(id+"F0.wireOp",EDGE,"E30.3")])],"isStart":false});
            var Q2;
            Q2=makeQuery(id+"F1.opExtrude","CAP_EDGE",EDGE,{"disambiguationData":[OSD([sQuery(id+"F0.wireOp",EDGE,"E30.4")])],"isStart":false});
            var Q3;
            Q3=makeQuery(id+"F1.opExtrude","CAP_EDGE",EDGE,{"disambiguationData":[OSD([sQuery(id+"F0.wireOp",EDGE,"E30.5")])],"isStart":false});
            var Q4;
            Q4=makeQuery(id+"F1.opExtrude","CAP_EDGE",EDGE,{"disambiguationData":[OSD([sQuery(id+"F0.wireOp",EDGE,"E22")])],"isStart":false});
            var Q5;
            Q5=makeQuery(id+"F1.opExtrude","CAP_EDGE",EDGE,{"disambiguationData":[OSD([sQuery(id+"F0.wireOp",EDGE,"E31.0")])],"isStart":false});
            var Q6;
            Q6=makeQuery(id+"F1.opExtrude","CAP_EDGE",EDGE,{"disambiguationData":[OSD([sQuery(id+"F0.wireOp",EDGE,"E31.1")])],"isStart":false});
            var Q7;
            Q7=makeQuery(id+"F1.opExtrude","CAP_EDGE",EDGE,{"disambiguationData":[OSD([sQuery(id+"F0.wireOp",EDGE,"E31.2")])],"isStart":false});
            var Q8;
            Q8=makeQuery(id+"F1.opExtrude","CAP_EDGE",EDGE,{"disambiguationData":[OSD([sQuery(id+"F0.wireOp",EDGE,"E22")])],"isStart":true});
            var Q9;
            Q9=makeQuery(id+"F1.opExtrude","CAP_EDGE",EDGE,{"disambiguationData":[OSD([sQuery(id+"F0.wireOp",EDGE,"E31.0")])],"isStart":true});
            var Q10;
            Q10=makeQuery(id+"F1.opExtrude","CAP_EDGE",EDGE,{"disambiguationData":[OSD([sQuery(id+"F0.wireOp",EDGE,"E31.1")])],"isStart":true});
            var Q11;
            Q11=makeQuery(id+"F1.opExtrude","CAP_EDGE",EDGE,{"disambiguationData":[OSD([sQuery(id+"F0.wireOp",EDGE,"E31.2")])],"isStart":true});
            var Q12;
            Q12=makeQuery(id+"F1.opExtrude","CAP_EDGE",EDGE,{"disambiguationData":[OSD([sQuery(id+"F0.wireOp",EDGE,"E36")])],"isStart":true});
            var Q13;
            Q13=makeQuery(id+"F1.opExtrude","CAP_EDGE",EDGE,{"disambiguationData":[OSD([sQuery(id+"F0.wireOp",EDGE,"E30.3")])],"isStart":true});
            var Q14;
            Q14=makeQuery(id+"F1.opExtrude","CAP_EDGE",EDGE,{"disambiguationData":[OSD([sQuery(id+"F0.wireOp",EDGE,"E30.4")])],"isStart":true});
            var Q15;
            Q15=makeQuery(id+"F1.opExtrude","CAP_EDGE",EDGE,{"disambiguationData":[OSD([sQuery(id+"F0.wireOp",EDGE,"E30.5")])],"isStart":true});
            chamfer(context, id + "F5", {"entities" : qUnion([Q0, Q1, Q2, Q3, Q4, Q5, Q6, Q7, Q8, Q9, Q10, Q11, Q12, Q13, Q14, Q15]), "width" : 1 * mm, "tangentPropagation" : true});
        }
        {
            var Q0;
            Q0=makeQuery(id+"F1.opExtrude","CAP_EDGE",EDGE,{"disambiguationData":[OSD([sQuery(id+"F0.wireOp",EDGE,"E123.MirrorCS")])],"isStart":false});
            var Q1;
            Q1=makeQuery(id+"F1.opExtrude","CAP_EDGE",EDGE,{"disambiguationData":[OSD([sQuery(id+"F0.wireOp",EDGE,"E131.MirrorCS")])],"isStart":false});
            var Q2;
            Q2=makeQuery(id+"F1.opExtrude","CAP_EDGE",EDGE,{"disambiguationData":[OSD([sQuery(id+"F0.wireOp",EDGE,"E125.MirrorCS")])],"isStart":false});
            var Q3;
            Q3=makeQuery(id+"F1.opExtrude","CAP_EDGE",EDGE,{"disambiguationData":[OSD([sQuery(id+"F0.wireOp",EDGE,"E129.MirrorCS")])],"isStart":false});
            var Q4;
            Q4=makeQuery(id+"F1.opExtrude","CAP_EDGE",EDGE,{"disambiguationData":[OSD([sQuery(id+"F0.wireOp",EDGE,"E140.MirrorCS")])],"isStart":false});
            var Q5;
            Q5=makeQuery(id+"F1.opExtrude","CAP_EDGE",EDGE,{"disambiguationData":[OSD([sQuery(id+"F0.wireOp",EDGE,"E132.MirrorCS")])],"isStart":false});
            var Q6;
            Q6=makeQuery(id+"F1.opExtrude","CAP_EDGE",EDGE,{"disambiguationData":[OSD([sQuery(id+"F0.wireOp",EDGE,"E137.MirrorCS")])],"isStart":false});
            var Q7;
            Q7=makeQuery(id+"F1.opExtrude","CAP_EDGE",EDGE,{"disambiguationData":[OSD([sQuery(id+"F0.wireOp",EDGE,"E146.MirrorCS")])],"isStart":false});
            var Q8;
            Q8=makeQuery(id+"F1.opExtrude","CAP_EDGE",EDGE,{"disambiguationData":[OSD([sQuery(id+"F0.wireOp",EDGE,"E132.MirrorCS")])],"isStart":true});
            var Q9;
            Q9=makeQuery(id+"F1.opExtrude","CAP_EDGE",EDGE,{"disambiguationData":[OSD([sQuery(id+"F0.wireOp",EDGE,"E137.MirrorCS")])],"isStart":true});
            var Q10;
            Q10=makeQuery(id+"F1.opExtrude","CAP_EDGE",EDGE,{"disambiguationData":[OSD([sQuery(id+"F0.wireOp",EDGE,"E140.MirrorCS")])],"isStart":true});
            var Q11;
            Q11=makeQuery(id+"F1.opExtrude","CAP_EDGE",EDGE,{"disambiguationData":[OSD([sQuery(id+"F0.wireOp",EDGE,"E146.MirrorCS")])],"isStart":true});
            var Q12;
            Q12=makeQuery(id+"F1.opExtrude","CAP_EDGE",EDGE,{"disambiguationData":[OSD([sQuery(id+"F0.wireOp",EDGE,"E131.MirrorCS")])],"isStart":true});
            var Q13;
            Q13=makeQuery(id+"F1.opExtrude","CAP_EDGE",EDGE,{"disambiguationData":[OSD([sQuery(id+"F0.wireOp",EDGE,"E123.MirrorCS")])],"isStart":true});
            var Q14;
            Q14=makeQuery(id+"F1.opExtrude","CAP_EDGE",EDGE,{"disambiguationData":[OSD([sQuery(id+"F0.wireOp",EDGE,"E125.MirrorCS")])],"isStart":true});
            var Q15;
            Q15=makeQuery(id+"F1.opExtrude","CAP_EDGE",EDGE,{"disambiguationData":[OSD([sQuery(id+"F0.wireOp",EDGE,"E129.MirrorCS")])],"isStart":true});
            chamfer(context, id + "F6", {"entities" : qUnion([Q0, Q1, Q2, Q3, Q4, Q5, Q6, Q7, Q8, Q9, Q10, Q11, Q12, Q13, Q14, Q15]), "width" : 1 * mm, "tangentPropagation" : true});
        }
        {
            var Q0;
            Q0=makeQuery(id+"F1.opExtrude","CAP_EDGE",EDGE,{"disambiguationData":[OSD([sQuery(id+"F0.wireOp",EDGE,"E64.MirrorCS")])],"isStart":false});
            var Q1;
            Q1=makeQuery(id+"F1.opExtrude","CAP_EDGE",EDGE,{"disambiguationData":[OSD([sQuery(id+"F0.wireOp",EDGE,"E57.MirrorCS")])],"isStart":false});
            var Q2;
            Q2=makeQuery(id+"F1.opExtrude","CAP_EDGE",EDGE,{"disambiguationData":[OSD([sQuery(id+"F0.wireOp",EDGE,"E66.MirrorCS")])],"isStart":false});
            var Q3;
            Q3=makeQuery(id+"F1.opExtrude","CAP_EDGE",EDGE,{"disambiguationData":[OSD([sQuery(id+"F0.wireOp",EDGE,"E70.MirrorCS")])],"isStart":false});
            var Q4;
            Q4=makeQuery(id+"F1.opExtrude","CAP_EDGE",EDGE,{"disambiguationData":[OSD([sQuery(id+"F0.wireOp",EDGE,"E63.MirrorCS")])],"isStart":false});
            var Q5;
            Q5=makeQuery(id+"F1.opExtrude","CAP_EDGE",EDGE,{"disambiguationData":[OSD([sQuery(id+"F0.wireOp",EDGE,"E69.MirrorCS")])],"isStart":false});
            var Q6;
            Q6=makeQuery(id+"F1.opExtrude","CAP_EDGE",EDGE,{"disambiguationData":[OSD([sQuery(id+"F0.wireOp",EDGE,"E68.MirrorCS")])],"isStart":false});
            var Q7;
            Q7=makeQuery(id+"F1.opExtrude","CAP_EDGE",EDGE,{"disambiguationData":[OSD([sQuery(id+"F0.wireOp",EDGE,"E56.MirrorCS")])],"isStart":false});
            var Q8;
            Q8=makeQuery(id+"F1.opExtrude","CAP_EDGE",EDGE,{"disambiguationData":[OSD([sQuery(id+"F0.wireOp",EDGE,"E69.MirrorCS")])],"isStart":true});
            var Q9;
            Q9=makeQuery(id+"F1.opExtrude","CAP_EDGE",EDGE,{"disambiguationData":[OSD([sQuery(id+"F0.wireOp",EDGE,"E63.MirrorCS")])],"isStart":true});
            var Q10;
            Q10=makeQuery(id+"F1.opExtrude","CAP_EDGE",EDGE,{"disambiguationData":[OSD([sQuery(id+"F0.wireOp",EDGE,"E70.MirrorCS")])],"isStart":true});
            var Q11;
            Q11=makeQuery(id+"F1.opExtrude","CAP_EDGE",EDGE,{"disambiguationData":[OSD([sQuery(id+"F0.wireOp",EDGE,"E66.MirrorCS")])],"isStart":true});
            var Q12;
            Q12=makeQuery(id+"F1.opExtrude","CAP_EDGE",EDGE,{"disambiguationData":[OSD([sQuery(id+"F0.wireOp",EDGE,"E64.MirrorCS")])],"isStart":true});
            var Q13;
            Q13=makeQuery(id+"F1.opExtrude","CAP_EDGE",EDGE,{"disambiguationData":[OSD([sQuery(id+"F0.wireOp",EDGE,"E57.MirrorCS")])],"isStart":true});
            var Q14;
            Q14=makeQuery(id+"F1.opExtrude","CAP_EDGE",EDGE,{"disambiguationData":[OSD([sQuery(id+"F0.wireOp",EDGE,"E56.MirrorCS")])],"isStart":true});
            var Q15;
            Q15=makeQuery(id+"F1.opExtrude","CAP_EDGE",EDGE,{"disambiguationData":[OSD([sQuery(id+"F0.wireOp",EDGE,"E68.MirrorCS")])],"isStart":true});
            chamfer(context, id + "F7", {"entities" : qUnion([Q0, Q1, Q2, Q3, Q4, Q5, Q6, Q7, Q8, Q9, Q10, Q11, Q12, Q13, Q14, Q15]), "width" : 1 * mm, "tangentPropagation" : true});
        }
        {
            var Q0;
            Q0=makeQuery(id+"F1.opExtrude","CAP_EDGE",EDGE,{"disambiguationData":[OSD([sQuery(id+"F0.wireOp",EDGE,"E138.MirrorCS")])],"isStart":false});
            var Q1;
            Q1=makeQuery(id+"F1.opExtrude","CAP_EDGE",EDGE,{"disambiguationData":[OSD([sQuery(id+"F0.wireOp",EDGE,"E143.MirrorCS")])],"isStart":false});
            var Q2;
            Q2=makeQuery(id+"F1.opExtrude","CAP_EDGE",EDGE,{"disambiguationData":[OSD([sQuery(id+"F0.wireOp",EDGE,"E149.MirrorCS")])],"isStart":false});
            var Q3;
            Q3=makeQuery(id+"F1.opExtrude","CAP_EDGE",EDGE,{"disambiguationData":[OSD([sQuery(id+"F0.wireOp",EDGE,"E127.MirrorCS")])],"isStart":false});
            var Q4;
            Q4=makeQuery(id+"F1.opExtrude","CAP_EDGE",EDGE,{"disambiguationData":[OSD([sQuery(id+"F0.wireOp",EDGE,"E134.MirrorCS")])],"isStart":false});
            var Q5;
            Q5=makeQuery(id+"F1.opExtrude","CAP_EDGE",EDGE,{"disambiguationData":[OSD([sQuery(id+"F0.wireOp",EDGE,"E144.MirrorCS")])],"isStart":false});
            var Q6;
            Q6=makeQuery(id+"F1.opExtrude","CAP_EDGE",EDGE,{"disambiguationData":[OSD([sQuery(id+"F0.wireOp",EDGE,"E139.MirrorCS")])],"isStart":false});
            var Q7;
            Q7=makeQuery(id+"F1.opExtrude","CAP_EDGE",EDGE,{"disambiguationData":[OSD([sQuery(id+"F0.wireOp",EDGE,"E133.MirrorCS")])],"isStart":false});
            var Q8;
            Q8=makeQuery(id+"F1.opExtrude","CAP_EDGE",EDGE,{"disambiguationData":[OSD([sQuery(id+"F0.wireOp",EDGE,"E127.MirrorCS")])],"isStart":true});
            var Q9;
            Q9=makeQuery(id+"F1.opExtrude","CAP_EDGE",EDGE,{"disambiguationData":[OSD([sQuery(id+"F0.wireOp",EDGE,"E143.MirrorCS")])],"isStart":true});
            var Q10;
            Q10=makeQuery(id+"F1.opExtrude","CAP_EDGE",EDGE,{"disambiguationData":[OSD([sQuery(id+"F0.wireOp",EDGE,"E134.MirrorCS")])],"isStart":true});
            var Q11;
            Q11=makeQuery(id+"F1.opExtrude","CAP_EDGE",EDGE,{"disambiguationData":[OSD([sQuery(id+"F0.wireOp",EDGE,"E138.MirrorCS")])],"isStart":true});
            var Q12;
            Q12=makeQuery(id+"F1.opExtrude","CAP_EDGE",EDGE,{"disambiguationData":[OSD([sQuery(id+"F0.wireOp",EDGE,"E149.MirrorCS")])],"isStart":true});
            var Q13;
            Q13=makeQuery(id+"F1.opExtrude","CAP_EDGE",EDGE,{"disambiguationData":[OSD([sQuery(id+"F0.wireOp",EDGE,"E144.MirrorCS")])],"isStart":true});
            var Q14;
            Q14=makeQuery(id+"F1.opExtrude","CAP_EDGE",EDGE,{"disambiguationData":[OSD([sQuery(id+"F0.wireOp",EDGE,"E139.MirrorCS")])],"isStart":true});
            var Q15;
            Q15=makeQuery(id+"F1.opExtrude","CAP_EDGE",EDGE,{"disambiguationData":[OSD([sQuery(id+"F0.wireOp",EDGE,"E133.MirrorCS")])],"isStart":true});
            chamfer(context, id + "F8", {"entities" : qUnion([Q0, Q1, Q2, Q3, Q4, Q5, Q6, Q7, Q8, Q9, Q10, Q11, Q12, Q13, Q14, Q15]), "width" : 1 * mm, "tangentPropagation" : true});
        }
        {
            var Q0;
            Q0=makeQuery(id+"F1.opExtrude","CAP_EDGE",EDGE,{"disambiguationData":[OSD([sQuery(id+"F0.wireOp",EDGE,"E211"),sQuery(id+"F0.wireOp",EDGE,"E213.MirrorCS")])],"isStart":false});
            var Q1;
            Q1=makeQuery(id+"F1.opExtrude","CAP_EDGE",EDGE,{"disambiguationData":[OSD([sQuery(id+"F0.wireOp",EDGE,"E212.MirrorCS")])],"isStart":false});
            var Q2;
            Q2=makeQuery(id+"F1.opExtrude","CAP_EDGE",EDGE,{"disambiguationData":[OSD([sQuery(id+"F0.wireOp",EDGE,"E210")])],"isStart":false});
            var Q3;
            Q3=makeQuery(id+"F1.opExtrude","CAP_EDGE",EDGE,{"disambiguationData":[OSD([sQuery(id+"F0.wireOp",EDGE,"E210")])],"isStart":true});
            var Q4;
            Q4=makeQuery(id+"F1.opExtrude","CAP_EDGE",EDGE,{"disambiguationData":[OSD([sQuery(id+"F0.wireOp",EDGE,"E211"),sQuery(id+"F0.wireOp",EDGE,"E213.MirrorCS")])],"isStart":true});
            var Q5;
            Q5=makeQuery(id+"F1.opExtrude","CAP_EDGE",EDGE,{"disambiguationData":[OSD([sQuery(id+"F0.wireOp",EDGE,"E212.MirrorCS")])],"isStart":true});
            var Q6;
            Q6=makeQuery(id+"F1.opExtrude","CAP_EDGE",EDGE,{"disambiguationData":[OSD([sQuery(id+"F0.wireOp",EDGE,"E215.MirrorCS"),sQuery(id+"F0.wireOp",EDGE,"E218.MirrorCS")])],"isStart":false});
            var Q7;
            Q7=makeQuery(id+"F1.opExtrude","CAP_EDGE",EDGE,{"disambiguationData":[OSD([sQuery(id+"F0.wireOp",EDGE,"E219.MirrorCS")])],"isStart":false});
            var Q8;
            Q8=makeQuery(id+"F1.opExtrude","CAP_EDGE",EDGE,{"disambiguationData":[OSD([sQuery(id+"F0.wireOp",EDGE,"E217.MirrorCS")])],"isStart":false});
            var Q9;
            Q9=makeQuery(id+"F1.opExtrude","CAP_EDGE",EDGE,{"disambiguationData":[OSD([sQuery(id+"F0.wireOp",EDGE,"E217.MirrorCS")])],"isStart":true});
            var Q10;
            Q10=makeQuery(id+"F1.opExtrude","CAP_EDGE",EDGE,{"disambiguationData":[OSD([sQuery(id+"F0.wireOp",EDGE,"E215.MirrorCS"),sQuery(id+"F0.wireOp",EDGE,"E218.MirrorCS")])],"isStart":true});
            var Q11;
            Q11=makeQuery(id+"F1.opExtrude","CAP_EDGE",EDGE,{"disambiguationData":[OSD([sQuery(id+"F0.wireOp",EDGE,"E219.MirrorCS")])],"isStart":true});
            var Q12;
            Q12=makeQuery(id+"F1.opExtrude","CAP_EDGE",EDGE,{"disambiguationData":[OSD([sQuery(id+"F0.wireOp",EDGE,"E161.MirrorCS"),sQuery(id+"F0.wireOp",EDGE,"E172.MirrorCS")])],"isStart":false});
            var Q13;
            Q13=makeQuery(id+"F1.opExtrude","CAP_EDGE",EDGE,{"disambiguationData":[OSD([sQuery(id+"F0.wireOp",EDGE,"E208")])],"isStart":false});
            var Q14;
            Q14=makeQuery(id+"F1.opExtrude","CAP_EDGE",EDGE,{"disambiguationData":[OSD([sQuery(id+"F0.wireOp",EDGE,"E209.MirrorC")])],"isStart":false});
            var Q15;
            Q15=makeQuery(id+"F1.opExtrude","CAP_EDGE",EDGE,{"disambiguationData":[OSD([sQuery(id+"F0.wireOp",EDGE,"E209.MirrorC")])],"isStart":true});
            var Q16;
            Q16=makeQuery(id+"F1.opExtrude","CAP_EDGE",EDGE,{"disambiguationData":[OSD([sQuery(id+"F0.wireOp",EDGE,"E208")])],"isStart":true});
            var Q17;
            Q17=makeQuery(id+"F1.opExtrude","CAP_EDGE",EDGE,{"disambiguationData":[OSD([sQuery(id+"F0.wireOp",EDGE,"E161.MirrorCS"),sQuery(id+"F0.wireOp",EDGE,"E172.MirrorCS")])],"isStart":true});
            var Q18;
            Q18=makeQuery(id+"F1.opExtrude","CAP_EDGE",EDGE,{"disambiguationData":[OSD([sQuery(id+"F0.wireOp",EDGE,"E160.MirrorCS"),sQuery(id+"F0.wireOp",EDGE,"E207.MirrorCS")])],"isStart":false});
            var Q19;
            Q19=makeQuery(id+"F1.opExtrude","CAP_EDGE",EDGE,{"disambiguationData":[OSD([sQuery(id+"F0.wireOp",EDGE,"E165.MirrorCS"),sQuery(id+"F0.wireOp",EDGE,"E171.MirrorCS")])],"isStart":false});
            var Q20;
            Q20=makeQuery(id+"F1.opExtrude","CAP_EDGE",EDGE,{"disambiguationData":[OSD([sQuery(id+"F0.wireOp",EDGE,"E196.MirrorCS")])],"isStart":false});
            var Q21;
            Q21=makeQuery(id+"F1.opExtrude","CAP_EDGE",EDGE,{"disambiguationData":[OSD([sQuery(id+"F0.wireOp",EDGE,"E196.MirrorCS")])],"isStart":true});
            var Q22;
            Q22=makeQuery(id+"F1.opExtrude","CAP_EDGE",EDGE,{"disambiguationData":[OSD([sQuery(id+"F0.wireOp",EDGE,"E162.MirrorCS")])],"isStart":true});
            var Q23;
            Q23=makeQuery(id+"F1.opExtrude","CAP_EDGE",EDGE,{"disambiguationData":[OSD([sQuery(id+"F0.wireOp",EDGE,"E162.MirrorCS")])],"isStart":false});
            var Q24;
            Q24=makeQuery(id+"F1.opExtrude","CAP_EDGE",EDGE,{"disambiguationData":[OSD([sQuery(id+"F0.wireOp",EDGE,"E189.MirrorCS")])],"isStart":false});
            var Q25;
            Q25=makeQuery(id+"F1.opExtrude","CAP_EDGE",EDGE,{"disambiguationData":[OSD([sQuery(id+"F0.wireOp",EDGE,"E189.MirrorCS")])],"isStart":true});
            var Q26;
            Q26=makeQuery(id+"F1.opExtrude","CAP_EDGE",EDGE,{"disambiguationData":[OSD([sQuery(id+"F0.wireOp",EDGE,"E147.MirrorCS")])],"isStart":true});
            var Q27;
            Q27=makeQuery(id+"F1.opExtrude","CAP_EDGE",EDGE,{"disambiguationData":[OSD([sQuery(id+"F0.wireOp",EDGE,"E147.MirrorCS")])],"isStart":false});
            var Q28;
            Q28=makeQuery(id+"F1.opExtrude","CAP_EDGE",EDGE,{"disambiguationData":[OSD([sQuery(id+"F0.wireOp",EDGE,"E20")])],"isStart":true});
            var Q29;
            Q29=makeQuery(id+"F1.opExtrude","CAP_EDGE",EDGE,{"disambiguationData":[OSD([sQuery(id+"F0.wireOp",EDGE,"E20")])],"isStart":false});
            var Q30;
            Q30=makeQuery(id+"F1.opExtrude","CAP_EDGE",EDGE,{"disambiguationData":[OSD([sQuery(id+"F0.wireOp",EDGE,"E193.MirrorCS")])],"isStart":true});
            var Q31;
            Q31=makeQuery(id+"F1.opExtrude","CAP_EDGE",EDGE,{"disambiguationData":[OSD([sQuery(id+"F0.wireOp",EDGE,"E193.MirrorCS")])],"isStart":false});
            var Q32;
            Q32=makeQuery(id+"F1.opExtrude","CAP_EDGE",EDGE,{"disambiguationData":[OSD([sQuery(id+"F0.wireOp",EDGE,"E165.MirrorCS"),sQuery(id+"F0.wireOp",EDGE,"E171.MirrorCS")])],"isStart":true});
            var Q33;
            Q33=makeQuery(id+"F1.opExtrude","CAP_EDGE",EDGE,{"disambiguationData":[OSD([sQuery(id+"F0.wireOp",EDGE,"E160.MirrorCS"),sQuery(id+"F0.wireOp",EDGE,"E207.MirrorCS")])],"isStart":true});
            var Q34;
            Q34=makeQuery(id+"F1.opExtrude","CAP_EDGE",EDGE,{"disambiguationData":[OSD([sQuery(id+"F0.wireOp",EDGE,"E206.MirrorCS")])],"isStart":true});
            var Q35;
            Q35=makeQuery(id+"F1.opExtrude","CAP_EDGE",EDGE,{"disambiguationData":[OSD([sQuery(id+"F0.wireOp",EDGE,"E206.MirrorCS")])],"isStart":false});
            var Q36;
            Q36=makeQuery(id+"F1.opExtrude","CAP_EDGE",EDGE,{"disambiguationData":[OSD([sQuery(id+"F0.wireOp",EDGE,"E205.MirrorCS")])],"isStart":true});
            var Q37;
            Q37=makeQuery(id+"F1.opExtrude","CAP_EDGE",EDGE,{"disambiguationData":[OSD([sQuery(id+"F0.wireOp",EDGE,"E205.MirrorCS")])],"isStart":false});
            var Q38;
            Q38=makeQuery(id+"F1.opExtrude","CAP_EDGE",EDGE,{"disambiguationData":[OSD([sQuery(id+"F0.wireOp",EDGE,"E154.MirrorCS")])],"isStart":true});
            var Q39;
            Q39=makeQuery(id+"F1.opExtrude","CAP_EDGE",EDGE,{"disambiguationData":[OSD([sQuery(id+"F0.wireOp",EDGE,"E154.MirrorCS")])],"isStart":false});
            var Q40;
            Q40=makeQuery(id+"F1.opExtrude","CAP_EDGE",EDGE,{"disambiguationData":[OSD([sQuery(id+"F0.wireOp",EDGE,"E186.MirrorCS")])],"isStart":true});
            var Q41;
            Q41=makeQuery(id+"F1.opExtrude","CAP_EDGE",EDGE,{"disambiguationData":[OSD([sQuery(id+"F0.wireOp",EDGE,"E186.MirrorCS")])],"isStart":false});
            var Q42;
            Q42=makeQuery(id+"F1.opExtrude","CAP_EDGE",EDGE,{"disambiguationData":[OSD([sQuery(id+"F0.wireOp",EDGE,"E130.MirrorCS")])],"isStart":true});
            var Q43;
            Q43=makeQuery(id+"F1.opExtrude","CAP_EDGE",EDGE,{"disambiguationData":[OSD([sQuery(id+"F0.wireOp",EDGE,"E130.MirrorCS")])],"isStart":false});
            var Q44;
            Q44=makeQuery(id+"F1.opExtrude","CAP_EDGE",EDGE,{"disambiguationData":[OSD([sQuery(id+"F0.wireOp",EDGE,"E170.MirrorCS")])],"isStart":false});
            var Q45;
            Q45=makeQuery(id+"F1.opExtrude","CAP_EDGE",EDGE,{"disambiguationData":[OSD([sQuery(id+"F0.wireOp",EDGE,"E170.MirrorCS")])],"isStart":true});
            var Q46;
            Q46=makeQuery(id+"F1.opExtrude","CAP_EDGE",EDGE,{"disambiguationData":[OSD([sQuery(id+"F0.wireOp",EDGE,"E216.MirrorCS")])],"isStart":false});
            var Q47;
            Q47=makeQuery(id+"F1.opExtrude","CAP_EDGE",EDGE,{"disambiguationData":[OSD([sQuery(id+"F0.wireOp",EDGE,"E216.MirrorCS")])],"isStart":true});
            var Q48;
            Q48=makeQuery(id+"F1.opExtrude","CAP_EDGE",EDGE,{"disambiguationData":[OSD([sQuery(id+"F0.wireOp",EDGE,"E214.MirrorCS")])],"isStart":false});
            var Q49;
            Q49=makeQuery(id+"F1.opExtrude","CAP_EDGE",EDGE,{"disambiguationData":[OSD([sQuery(id+"F0.wireOp",EDGE,"E214.MirrorCS")])],"isStart":true});
            var Q50;
            Q50=makeQuery(id+"F1.opExtrude","CAP_EDGE",EDGE,{"disambiguationData":[OSD([sQuery(id+"F0.wireOp",EDGE,"E76.MirrorCS")])],"isStart":true});
            var Q51;
            Q51=makeQuery(id+"F1.opExtrude","CAP_EDGE",EDGE,{"disambiguationData":[OSD([sQuery(id+"F0.wireOp",EDGE,"E76.MirrorCS")])],"isStart":false});
            var Q52;
            Q52=makeQuery(id+"F1.opExtrude","CAP_EDGE",EDGE,{"disambiguationData":[OSD([sQuery(id+"F0.wireOp",EDGE,"E65.MirrorCS")])],"isStart":false});
            var Q53;
            Q53=makeQuery(id+"F1.opExtrude","CAP_EDGE",EDGE,{"disambiguationData":[OSD([sQuery(id+"F0.wireOp",EDGE,"E65.MirrorCS")])],"isStart":true});
            var Q54;
            Q54=makeQuery(id+"F1.opExtrude","CAP_EDGE",EDGE,{"disambiguationData":[OSD([sQuery(id+"F0.wireOp",EDGE,"E82.MirrorCS")])],"isStart":true});
            var Q55;
            Q55=makeQuery(id+"F1.opExtrude","CAP_EDGE",EDGE,{"disambiguationData":[OSD([sQuery(id+"F0.wireOp",EDGE,"E82.MirrorCS")])],"isStart":false});
            var Q56;
            Q56=makeQuery(id+"F1.opExtrude","CAP_EDGE",EDGE,{"disambiguationData":[OSD([sQuery(id+"F0.wireOp",EDGE,"E75.MirrorCS")])],"isStart":false});
            var Q57;
            Q57=makeQuery(id+"F1.opExtrude","CAP_EDGE",EDGE,{"disambiguationData":[OSD([sQuery(id+"F0.wireOp",EDGE,"E75.MirrorCS")])],"isStart":true});
            var Q58;
            Q58=makeQuery(id+"F1.opExtrude","CAP_EDGE",EDGE,{"disambiguationData":[OSD([sQuery(id+"F0.wireOp",EDGE,"E79.MirrorCS")])],"isStart":false});
            var Q59;
            Q59=makeQuery(id+"F1.opExtrude","CAP_EDGE",EDGE,{"disambiguationData":[OSD([sQuery(id+"F0.wireOp",EDGE,"E79.MirrorCS")])],"isStart":true});
            var Q60;
            Q60=makeQuery(id+"F1.opExtrude","CAP_EDGE",EDGE,{"disambiguationData":[OSD([sQuery(id+"F0.wireOp",EDGE,"E71.MirrorCS"),sQuery(id+"F0.wireOp",EDGE,"E94.MirrorCS")])],"isStart":true});
            var Q61;
            Q61=makeQuery(id+"F1.opExtrude","CAP_EDGE",EDGE,{"disambiguationData":[OSD([sQuery(id+"F0.wireOp",EDGE,"E71.MirrorCS"),sQuery(id+"F0.wireOp",EDGE,"E94.MirrorCS")])],"isStart":false});
            var Q62;
            Q62=makeQuery(id+"F1.opExtrude","CAP_EDGE",EDGE,{"disambiguationData":[OSD([sQuery(id+"F0.wireOp",EDGE,"E21"),sQuery(id+"F0.wireOp",EDGE,"E86.MirrorCS")])],"isStart":true});
            var Q63;
            Q63=makeQuery(id+"F1.opExtrude","CAP_EDGE",EDGE,{"disambiguationData":[OSD([sQuery(id+"F0.wireOp",EDGE,"E21"),sQuery(id+"F0.wireOp",EDGE,"E86.MirrorCS")])],"isStart":false});
            var Q64;
            Q64=makeQuery(id+"F1.opExtrude","CAP_EDGE",EDGE,{"disambiguationData":[OSD([sQuery(id+"F0.wireOp",EDGE,"E18"),sQuery(id+"F0.wireOp",EDGE,"E38.0")])],"isStart":false});
            var Q65;
            Q65=makeQuery(id+"F1.opExtrude","CAP_EDGE",EDGE,{"disambiguationData":[OSD([sQuery(id+"F0.wireOp",EDGE,"E18"),sQuery(id+"F0.wireOp",EDGE,"E38.0")])],"isStart":true});
            var Q66;
            Q66=makeQuery(id+"F1.opExtrude","CAP_EDGE",EDGE,{"disambiguationData":[OSD([sQuery(id+"F0.wireOp",EDGE,"E38.1")])],"isStart":true});
            var Q67;
            Q67=makeQuery(id+"F1.opExtrude","CAP_EDGE",EDGE,{"disambiguationData":[OSD([sQuery(id+"F0.wireOp",EDGE,"E38.1")])],"isStart":false});
            var Q68;
            Q68=makeQuery(id+"F1.opExtrude","CAP_EDGE",EDGE,{"disambiguationData":[OSD([sQuery(id+"F0.wireOp",EDGE,"E38.2")])],"isStart":false});
            var Q69;
            Q69=makeQuery(id+"F1.opExtrude","CAP_EDGE",EDGE,{"disambiguationData":[OSD([sQuery(id+"F0.wireOp",EDGE,"E38.2")])],"isStart":true});
            var Q70;
            Q70=makeQuery(id+"F1.opExtrude","CAP_EDGE",EDGE,{"disambiguationData":[OSD([sQuery(id+"F0.wireOp",EDGE,"E38.3")])],"isStart":false});
            var Q71;
            Q71=makeQuery(id+"F1.opExtrude","CAP_EDGE",EDGE,{"disambiguationData":[OSD([sQuery(id+"F0.wireOp",EDGE,"E38.3")])],"isStart":true});
            var Q72;
            Q72=makeQuery(id+"F1.opExtrude","CAP_EDGE",EDGE,{"disambiguationData":[OSD([sQuery(id+"F0.wireOp",EDGE,"E38.4")])],"isStart":true});
            var Q73;
            Q73=makeQuery(id+"F1.opExtrude","CAP_EDGE",EDGE,{"disambiguationData":[OSD([sQuery(id+"F0.wireOp",EDGE,"E38.4")])],"isStart":false});
            var Q74;
            Q74=makeQuery(id+"F1.opExtrude","CAP_EDGE",EDGE,{"disambiguationData":[OSD([sQuery(id+"F0.wireOp",EDGE,"E19")])],"isStart":false});
            var Q75;
            Q75=makeQuery(id+"F1.opExtrude","CAP_EDGE",EDGE,{"disambiguationData":[OSD([sQuery(id+"F0.wireOp",EDGE,"E19")])],"isStart":true});
            chamfer(context, id + "F9", {"entities" : qUnion([Q0, Q1, Q2, Q3, Q4, Q5, Q6, Q7, Q8, Q9, Q10, Q11, Q12, Q13, Q14, Q15, Q16, Q17, Q18, Q19, Q20, Q21, Q22, Q23, Q24, Q25, Q26, Q27, Q28, Q29, Q30, Q31, Q32, Q33, Q34, Q35, Q36, Q37, Q38, Q39, Q40, Q41, Q42, Q43, Q44, Q45, Q46, Q47, Q48, Q49, Q50, Q51, Q52, Q53, Q54, Q55, Q56, Q57, Q58, Q59, Q60, Q61, Q62, Q63, Q64, Q65, Q66, Q67, Q68, Q69, Q70, Q71, Q72, Q73, Q74, Q75]), "width" : 1 * mm, "tangentPropagation" : true});
        }
    });
